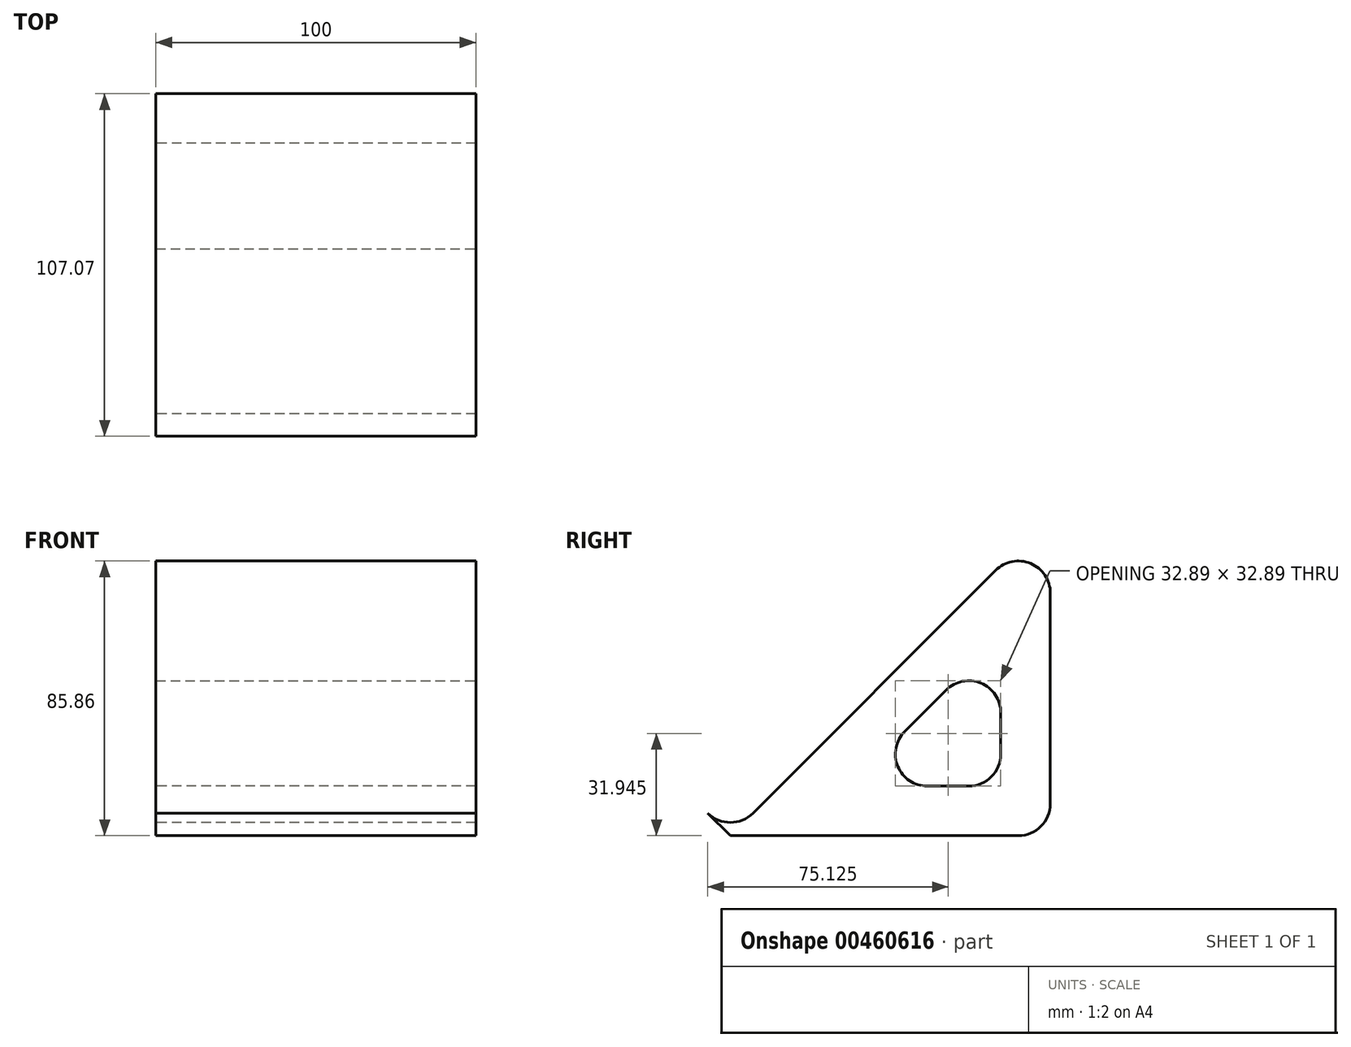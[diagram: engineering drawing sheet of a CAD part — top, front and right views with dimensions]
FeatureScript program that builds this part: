
annotation { "Feature Type Name" : "Feature", "Feature Type Description" : "" }
export const myFeature = defineFeature(function(context is Context, id is Id, definition is map)
    precondition{}
    {
        {
            var Q0;
            Q0=qCreatedBy(makeId("Right.planeOp"),FACE);
            var sketch = newSketch(context, id + "F0", { "sketchPlane" : qUnion([Q0])});
            skLineSegment(sketch, "E0.top", {"start": v(50, -50) * mm, "end": v(-50, -50) * mm});
            skLineSegment(sketch, "E0.left", {"start": v(50, 50) * mm, "end": v(50, -50) * mm});
            skPoint(sketch, "E0.middle", {"position": v(0, 0) * mm});
            skLineSegment(sketch, "E1", {"start": v(-50, -50) * mm, "end": v(50, 50) * mm});
            skLineSegment(sketch, "E2", {"start": v(-50, -50) * mm, "end": v(-42.93, -42.93) * mm, "construction": true});
            skLineSegment(sketch, "E3", {"start": v(-50, -50) * mm, "end": v(-57.07, -42.93) * mm});
            skArc(sketch, "E4", {"start": v(-57.07, -42.93) * mm, "mid": v(-50, -45.86) * mm, "end": v(-42.93, -42.93) * mm});
            skLineSegment(sketch, "E5.0", {"start": v(-12.58, -34.5) * mm, "end": v(34.5, 12.58) * mm});
            skLineSegment(sketch, "E5.1", {"start": v(34.5, -34.5) * mm, "end": v(-12.58, -34.5) * mm});
            skLineSegment(sketch, "E5.2", {"start": v(34.5, 12.58) * mm, "end": v(34.5, -34.5) * mm});
            skSolve(sketch);
        }
        {
            var Q0;
            {var subQ3=sQuery(id+"F0.wireOp",EDGE,"E0.top");Q0=makeQuery(id+"F0.imprint","IMPRINT",FACE,{"disambiguationData":[TD([[makeQuery(id+"F0.imprint","IMPRINT",EDGE,{"derivedFrom":subQ3}),-1.0]])]});}
            var Q1;
            {var subQ0=sQuery(id+"F0.wireOp",EDGE,"E3");Q1=makeQuery(id+"F0.imprint","IMPRINT",FACE,{"disambiguationData":[TD([[makeQuery(id+"F0.imprint","IMPRINT",EDGE,{"derivedFrom":subQ0}),-1.0]])]});}
            extrude(context, id + "F1", {"entities" : qUnion([Q0, Q1]), "depth" : 100 * mm});
        }
        {
            var Q0;
            Q0=makeQuery(id+"F1.opExtrude","SWEPT_EDGE",EDGE,{"disambiguationData":[OSD([sQuery(id+"F0.wireOp",EDGE,"E0.left"),sQuery(id+"F0.wireOp",EDGE,"E1")])]});
            var Q1;
            Q1=makeQuery(id+"F1.opExtrude","SWEPT_EDGE",EDGE,{"disambiguationData":[OSD([sQuery(id+"F0.wireOp",EDGE,"E5.0"),sQuery(id+"F0.wireOp",EDGE,"E5.2")])]});
            var Q2;
            Q2=makeQuery(id+"F1.opExtrude","SWEPT_EDGE",EDGE,{"disambiguationData":[OSD([sQuery(id+"F0.wireOp",EDGE,"E0.top"),sQuery(id+"F0.wireOp",EDGE,"E0.left")])]});
            var Q3;
            Q3=makeQuery(id+"F1.opExtrude","SWEPT_EDGE",EDGE,{"disambiguationData":[OSD([sQuery(id+"F0.wireOp",EDGE,"E5.1"),sQuery(id+"F0.wireOp",EDGE,"E5.2")])]});
            var Q4;
            Q4=makeQuery(id+"F1.opExtrude","SWEPT_EDGE",EDGE,{"disambiguationData":[OSD([sQuery(id+"F0.wireOp",EDGE,"E5.0"),sQuery(id+"F0.wireOp",EDGE,"E5.1")])]});
            fillet(context, id + "F2", {"entities" : qUnion([Q0, Q1, Q2, Q3, Q4]), "radius" : 10 * mm, "tangentPropagation" : true, "allowEdgeOverflow" : false});
        }
    });
